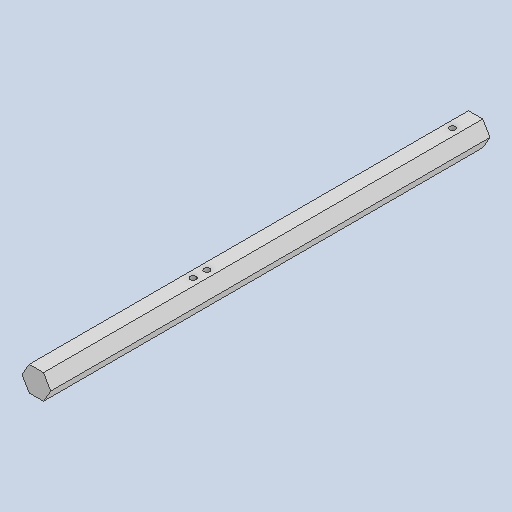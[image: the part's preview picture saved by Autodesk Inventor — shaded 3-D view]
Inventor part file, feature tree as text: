
AUTODESK INVENTOR PART (.ipt)
format: ipt  version: 2022 (Build 260153000, 153)  size: 122,368 bytes
history: native  units: mm
features: other x4, reference x3, extrude x2, sketch x2
ambient origin geometry x8: Origin, YZ Plane, XZ Plane, XY Plane, X Axis, Y Axis, Z Axis, Center Point
bodies: Solid1 (feature_tree)
feature tree (11):
  extrude  "Extrusion1"  Depth=3.1mm TaperAngle=360.0deg
  extrude  "Extrusion2"  Depth=10.0mm
  sketch  "Sketch1"  dims[d0=3.1mm d1=60.0mm d3=360.0deg]
  reference  "Reference1"
  reference  "Reference2"
  sketch  "Sketch2"  dims[d5=95.0mm d6=0.0mm d7=1.3mm d8=3.0mm d9=33.9mm d10=5.0mm d11=10.0mm d12=0.0mm]
  reference  "Reference3"
  other  "<userpath>\OneDrive\Escritorio\Mini_Proyecto_Diseno\Diseno_18012\Modelo_MPD\caja_nuevo.iam"
  other  "caja_nuevo.iam"
  other  "Rodamiento_Ejes:8"
  other  "hombro_nuevo:6"
